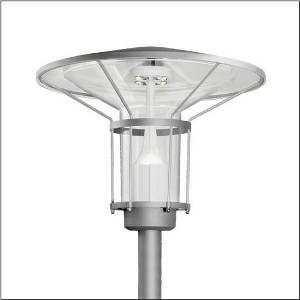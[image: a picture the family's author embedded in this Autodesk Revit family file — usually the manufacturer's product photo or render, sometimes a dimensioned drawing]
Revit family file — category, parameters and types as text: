
# Revit family: laterne_classic_iq___pl1_2s_5xa5245of14h_0553
name_source: partatom
category: Lighting Fixtures
units: mm (PartAtom-declared; Revit-internal decimal feet)

## family parameters
Cut with Voids When Loaded = No
Host = Face
Light Source = No
Part Type = Normal
Room Calculation Point = No
Round Connector Dimension = Use Diameter
Shared = No

## types (1)
- --- (1 x LED, 2670 lm, 21.8 W, 2700K)
    Apparent Load = 22 VA
    CIE Flux Codes = 21 60 93 97 100
    Color Rendering = 70
    Color Temperature = 2700K
    Default Elevation = 1800 mm
    Description = Lantern Classic iQ, mast luminaire, Module 540 iQ-SR, primary light control with 3 zone facetted reflector, of plastic, silver coated, highly specular, structured, primary optical cover: cover, of PMMA, transparent, light distribution: PL1.2s, light emission: direct distribution, primary light characteristic: symmetric, installation type: post-top, LED, High Power LED, rated luminous flux: 2.970lm, luminous efficacy: 136lm/W, light colour: 727, colour temperature: 2700K, control gear: iQ Street-Remote, control: pre-setting: logarithmic dimming characteristic, Street-Remote, Auto-Match, Temp-Guard, Lumen-Switch, Night-Set, Smart-Wire, Light-Fading, Desk-Remote (wireless, voltage-free reading and setting of iQ features in the workshop via application-optimized NFC function/RFID function), optimised constant luminous flux control (CLO 2.0), with terminal, 6-pole, max. 2.5mm², mains connection: 230..240V, AC, 50/60Hz, start of lifetime: 22W, end of service life: 23W, reduction: 11W, luminaire housing, upper part, of glass-fibre reinforced polyester, coated, Siteco® metallic grey (DB 702S), diameter: 750mm, height: 596mm, spigot size: d x l = 76 x 70mm (post-top) | with reducer (optional accessory) 60 x 70mm, mounting height: 3..5m, post-top mast mounting element, of diecast aluminium, coated, Siteco® metallic grey (DB 702S), Module 540 iQ-SR, traffic white (RAL 9016), equipment: standard, protection rating (complete): IP65, insulation class (complete): insulation class II (safety insulation), certification: CE, ENEC, VDE, packaging unit: 1 piece

Light Distribution: PL1.2s
    Height = 596 mm
    Lamp = 1 x LED
    Lamp Light Flux = 2670 lm
    Lamp Power = 21.8 W
    Lamp count = 1
    Length = 750 mm
    Luminous efficacy = 122 lm/W
    Manufacturer = Siteco
    ModVariant = No
    Model = 5XA5245OF14H
    Number of Poles = 1
    OnlyDefault = Yes
    Power Factor = 1
    Product Name = Laterne Classic iQ | PL1.2s
    Product group = mast luminaire | pylon top
    ProductGroupID = 6100
    Protection Class = Protection class II
    Protection Degree = IP 65
    RLX_Detail_Level = 1
    RLX_Emergency_Light_Flux = 0 lm
    RLX_Emergency_Type = 0
    RLX_Emergency_Type_DB = No
    RlxData = <blob elided: 37757 chars, md5=1cb56142>
    Socket = socket
    Standby Power = 0 W
    System Light Flux = 2670 lm
    System Power = 22 W
    Type Comments = factory setting: luminous flux: 100 % | dim-lin: 254 | 456 mA
    Type Image = l_1006052.jpg
    URL = http://relux.com
    VarID = @adj_167111
    Voltage = 0 V
    Weight = 0.00 kg
    Width = 0 mm  [stored 0 ft]

note: [stored X ft] marks values corroborated as IEEE doubles in the binary element streams (Revit-internal decimal feet)

## geometry (parser evidence)
native form markers: Blend x4, Sweep x10
no freeform markers — native parametric forms only
